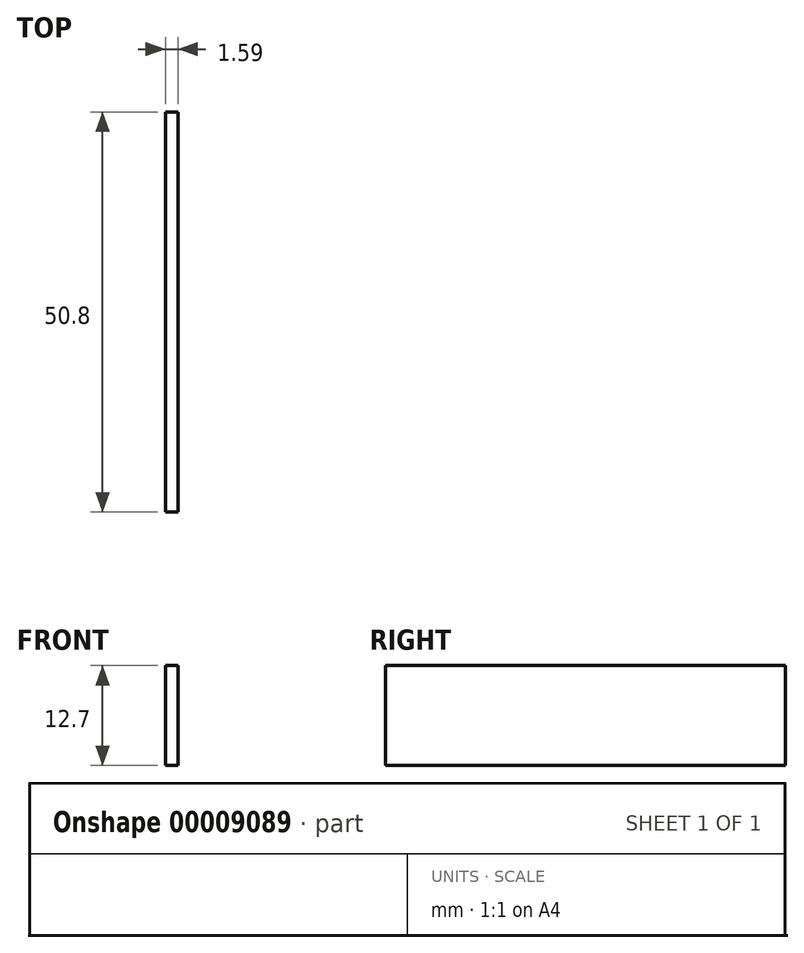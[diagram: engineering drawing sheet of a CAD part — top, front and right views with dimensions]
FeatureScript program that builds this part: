
annotation { "Feature Type Name" : "Feature", "Feature Type Description" : "" }
export const myFeature = defineFeature(function(context is Context, id is Id, definition is map)
    precondition{}
    {
        {
            var Q0;
            Q0=qCreatedBy(makeId("Top.planeOp"),FACE);
            var sketch = newSketch(context, id + "F0", { "sketchPlane" : qUnion([Q0])});
            skLineSegment(sketch, "E0.bottom", {"start": v(0, 0) * mm, "end": v(11.11, 0) * mm});
            skLineSegment(sketch, "E0.top", {"start": v(0, 287.37) * mm, "end": v(11.11, 287.37) * mm});
            skLineSegment(sketch, "E0.left", {"start": v(0, 0) * mm, "end": v(0, 287.37) * mm});
            skLineSegment(sketch, "E0.right", {"start": v(11.11, 0) * mm, "end": v(11.11, 287.37) * mm});
            skCircle(sketch, "E1", {"center": v(7.3, 50.8) * mm, "radius": 2.54 * mm});
            skCircle(sketch, "E2", {"center": v(7.3, 185.77) * mm, "radius": 2.54 * mm});
            skLineSegment(sketch, "E3.bottom", {"start": v(0, 287.37) * mm, "end": v(-1.59, 287.37) * mm});
            skLineSegment(sketch, "E3.top", {"start": v(0, 0) * mm, "end": v(-1.59, 0) * mm});
            skLineSegment(sketch, "E3.left", {"start": v(0, 287.37) * mm, "end": v(0, 0) * mm});
            skLineSegment(sketch, "E3.right", {"start": v(-1.59, 287.37) * mm, "end": v(-1.59, 0) * mm});
            skLineSegment(sketch, "E4.bottom", {"start": v(11.11, 25.4) * mm, "end": v(-1.59, 25.4) * mm});
            skLineSegment(sketch, "E4.top", {"start": v(11.11, 76.2) * mm, "end": v(-1.59, 76.2) * mm});
            skLineSegment(sketch, "E4.left", {"start": v(11.11, 25.4) * mm, "end": v(11.11, 76.2) * mm});
            skLineSegment(sketch, "E4.right", {"start": v(-1.59, 25.4) * mm, "end": v(-1.59, 76.2) * mm});
            skLineSegment(sketch, "E5.bottom", {"start": v(-1.59, 160.37) * mm, "end": v(11.11, 160.37) * mm});
            skLineSegment(sketch, "E5.top", {"start": v(-1.59, 211.17) * mm, "end": v(11.11, 211.17) * mm});
            skLineSegment(sketch, "E5.left", {"start": v(-1.59, 160.37) * mm, "end": v(-1.59, 211.17) * mm});
            skLineSegment(sketch, "E5.right", {"start": v(11.11, 160.37) * mm, "end": v(11.11, 211.17) * mm});
            skLineSegment(sketch, "E6", {"start": v(0, 261.97) * mm, "end": v(-1.59, 261.97) * mm});
            skPoint(sketch, "E7", {"position": v(11.11, 143.68) * mm});
            skPoint(sketch, "E8", {"position": v(0, 143.68) * mm});
            skLineSegment(sketch, "E9", {"start": v(7.3, 188.3) * mm, "end": v(2.54, 188.3) * mm});
            skLineSegment(sketch, "E10", {"start": v(7.3, 183.23) * mm, "end": v(2.54, 183.23) * mm});
            skArc(sketch, "E11", {"start": v(2.54, 188.3) * mm, "mid": v(0, 185.77) * mm, "end": v(2.54, 183.23) * mm});
            skLineSegment(sketch, "E12", {"start": v(7.3, 48.26) * mm, "end": v(2.54, 48.26) * mm});
            skLineSegment(sketch, "E13", {"start": v(0, 50.8) * mm, "end": v(0, 50.8) * mm});
            skLineSegment(sketch, "E14", {"start": v(2.54, 53.34) * mm, "end": v(7.3, 53.34) * mm});
            skPoint(sketch, "E15.visualSharp", {"position": v(0, 53.34) * mm});
            skArc(sketch, "E15.filletArc", {"start": v(2.54, 53.34) * mm, "mid": v(0.74, 52.6) * mm, "end": v(0, 50.8) * mm});
            skPoint(sketch, "E16.visualSharp", {"position": v(0, 48.26) * mm});
            skArc(sketch, "E16.filletArc", {"start": v(0, 50.8) * mm, "mid": v(0.74, 49) * mm, "end": v(2.54, 48.26) * mm});
            skSolve(sketch);
        }
        {
            var Q0;
            {var subQ0=sQuery(id+"F0.wireOp",EDGE,"E6");Q0=makeQuery(id+"F0.imprint","IMPRINT",FACE,{"disambiguationData":[TD([[makeQuery(id+"F0.imprint","IMPRINT",EDGE,{"derivedFrom":subQ0}),1.0]])]});}
            var Q1;
            {var subQ0=sQuery(id+"F0.wireOp",EDGE,"E5.left");Q1=makeQuery(id+"F0.imprint","IMPRINT",FACE,{"disambiguationData":[TD([[makeQuery(id+"F0.imprint","IMPRINT",EDGE,{"derivedFrom":subQ0}),-1.0]])]});}
            var Q2;
            {var subQ0=sQuery(id+"F0.wireOp",EDGE,"E4.right");Q2=makeQuery(id+"F0.imprint","IMPRINT",FACE,{"disambiguationData":[TD([[makeQuery(id+"F0.imprint","IMPRINT",EDGE,{"derivedFrom":subQ0}),-1.0]])]});}
            var Q3;
            {var subQ0=sQuery(id+"F0.wireOp",EDGE,"E5.bottom");var subQ1=sQuery(id+"F0.wireOp",EDGE,"E3.left");var subQ2=makeQuery(id+"F0.imprint","INTERSECT",VERTEX,{"derivedFrom":[subQ1,subQ0]});Q3=makeQuery(id+"F0.imprint","IMPRINT",FACE,{"disambiguationData":[TD([[makeQuery(id+"F0.imprint","IMPRINT",EDGE,{"disambiguationData":[TD([[subQ2,-1.0]])],"derivedFrom":subQ1}),-1.0]])]});}
            extrude(context, id + "F1", {"entities" : qUnion([Q0, Q1, Q2, Q3]), "oppositeDirection" : true, "depth" : 11.1 * mm});
        }
        {
            var Q0;
            {var subQ0=sQuery(id+"F0.wireOp",EDGE,"E5.bottom");var subQ1=sQuery(id+"F0.wireOp",EDGE,"E3.left");var subQ2=makeQuery(id+"F0.imprint","INTERSECT",VERTEX,{"derivedFrom":[subQ1,subQ0]});Q0=makeQuery(id+"F0.imprint","IMPRINT",FACE,{"disambiguationData":[TD([[makeQuery(id+"F0.imprint","IMPRINT",EDGE,{"disambiguationData":[TD([[subQ2,-1.0]])],"derivedFrom":subQ1}),-1.0]])]});}
            var Q1;
            {var subQ0=sQuery(id+"F0.wireOp",EDGE,"E4.right");Q1=makeQuery(id+"F0.imprint","IMPRINT",FACE,{"disambiguationData":[TD([[makeQuery(id+"F0.imprint","IMPRINT",EDGE,{"derivedFrom":subQ0}),-1.0]])]});}
            var Q2;
            {var subQ0=sQuery(id+"F0.wireOp",EDGE,"E5.left");Q2=makeQuery(id+"F0.imprint","IMPRINT",FACE,{"disambiguationData":[TD([[makeQuery(id+"F0.imprint","IMPRINT",EDGE,{"derivedFrom":subQ0}),-1.0]])]});}
            var Q3;
            {var subQ0=sQuery(id+"F0.wireOp",EDGE,"E6");Q3=makeQuery(id+"F0.imprint","IMPRINT",FACE,{"disambiguationData":[TD([[makeQuery(id+"F0.imprint","IMPRINT",EDGE,{"derivedFrom":subQ0}),1.0]])]});}
            var Q4;
            {var subQ5=sQuery(id+"F0.wireOp",EDGE,"E5.right");Q4=makeQuery(id+"F0.imprint","IMPRINT",FACE,{"disambiguationData":[TD([[makeQuery(id+"F0.imprint","IMPRINT",EDGE,{"derivedFrom":subQ5}),1.0]])]});}
            var Q5;
            {var subQ4=sQuery(id+"F0.wireOp",EDGE,"E4.left");Q5=makeQuery(id+"F0.imprint","IMPRINT",FACE,{"disambiguationData":[TD([[makeQuery(id+"F0.imprint","IMPRINT",EDGE,{"derivedFrom":subQ4}),1.0]])]});}
            extrude(context, id + "F2", {"entities" : qUnion([Q0, Q1, Q2, Q3, Q4, Q5]), "operationType" : NewBodyOperationType.ADD, "depth" : 1.59 * mm});
        }
    });
